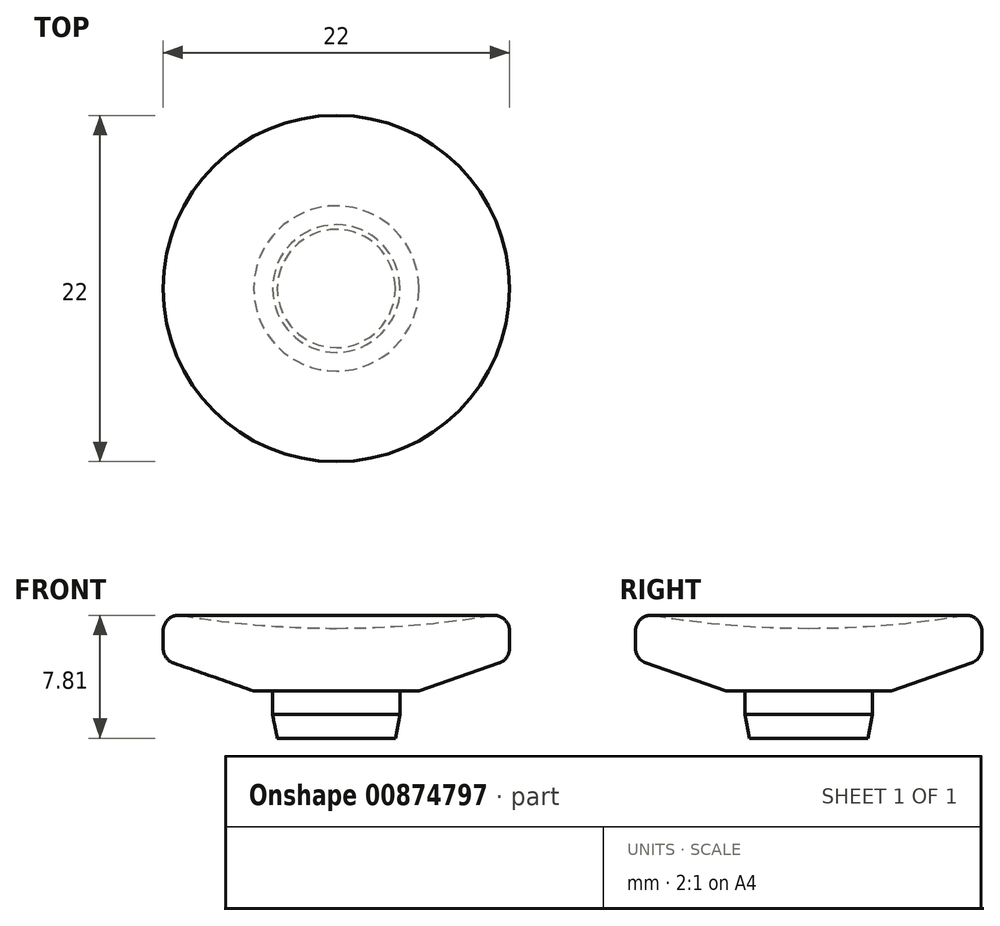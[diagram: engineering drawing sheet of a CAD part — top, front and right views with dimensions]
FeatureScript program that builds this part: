
annotation { "Feature Type Name" : "Feature", "Feature Type Description" : "" }
export const myFeature = defineFeature(function(context is Context, id is Id, definition is map)
    precondition{}
    {
        {
            var Q0;
            Q0=qCreatedBy(makeId("Front.planeOp"),FACE);
            var sketch = newSketch(context, id + "F0", { "sketchPlane" : qUnion([Q0])});
            skLineSegment(sketch, "E0", {"start": v(0, -3.57) * mm, "end": v(0, 7.12) * mm, "construction": true});
            skLineSegment(sketch, "E1", {"start": v(0, 0) * mm, "end": v(4.05, 0) * mm});
            skLineSegment(sketch, "E2", {"start": v(4.05, 0) * mm, "end": v(4.05, 3) * mm});
            skLineSegment(sketch, "E3", {"start": v(4.05, 3) * mm, "end": v(5.25, 3) * mm});
            skLineSegment(sketch, "E4", {"start": v(5.25, 3) * mm, "end": v(11, 5) * mm});
            skLineSegment(sketch, "E5", {"start": v(11, 5) * mm, "end": v(11, 8) * mm});
            skArc(sketch, "E6", {"start": v(11, 8) * mm, "mid": v(5.52, 7.24) * mm, "end": v(0, 6.98) * mm});
            skLineSegment(sketch, "E7.trimOffspring", {"start": v(0, 6.98) * mm, "end": v(0, 0) * mm});
            skPoint(sketch, "E8.start.orphan", {"position": v(0, 8) * mm});
            skSolve(sketch);
        }
        {
            var Q0;
            Q0 = qSketchRegion(id + "F0", true);
            var Q1;
            Q1=sQuery(id+"F0.wireOp",EDGE,"E0");
            revolve(context, id + "F1", {"surfaceOperationType" : NewSurfaceOperationType.NEW, "entities" : qUnion([Q0]), "axis" : qUnion([Q1]), "revolveType" : RevolveType.FULL});
        }
        {
            var Q0;
            Q0=makeQuery(id+"F1.opRevolve","SWEPT_EDGE",EDGE,{"disambiguationData":[OSD([sQuery(id+"F0.wireOp",EDGE,"E5"),sQuery(id+"F0.wireOp",EDGE,"33tfvtyz-JtyN-Mw5L-3XGJ-TJyQ87O0g8P3")])]});
            var Q1;
            Q1=makeQuery(id+"F1.opRevolve","SWEPT_EDGE",EDGE,{"disambiguationData":[OSD([sQuery(id+"F0.wireOp",EDGE,"E4"),sQuery(id+"F0.wireOp",EDGE,"E5")])]});
            fillet(context, id + "F2", {"entities" : qUnion([Q0, Q1]), "radius" : 1 * mm, "tangentPropagation" : true, "allowEdgeOverflow" : false});
        }
        {
            var Q0;
            Q0=makeQuery(id+"F1.opRevolve","SWEPT_EDGE",EDGE,{"disambiguationData":[OSD([sQuery(id+"F0.wireOp",EDGE,"E1"),sQuery(id+"F0.wireOp",EDGE,"E2")])]});
            chamfer(context, id + "F3", {"entities" : qUnion([Q0]), "chamferType" : ChamferType.TWO_OFFSETS, "width1" : .3 * mm, "oppositeDirection" : false, "width2" : 1.5 * mm, "tangentPropagation" : true});
        }
    });
